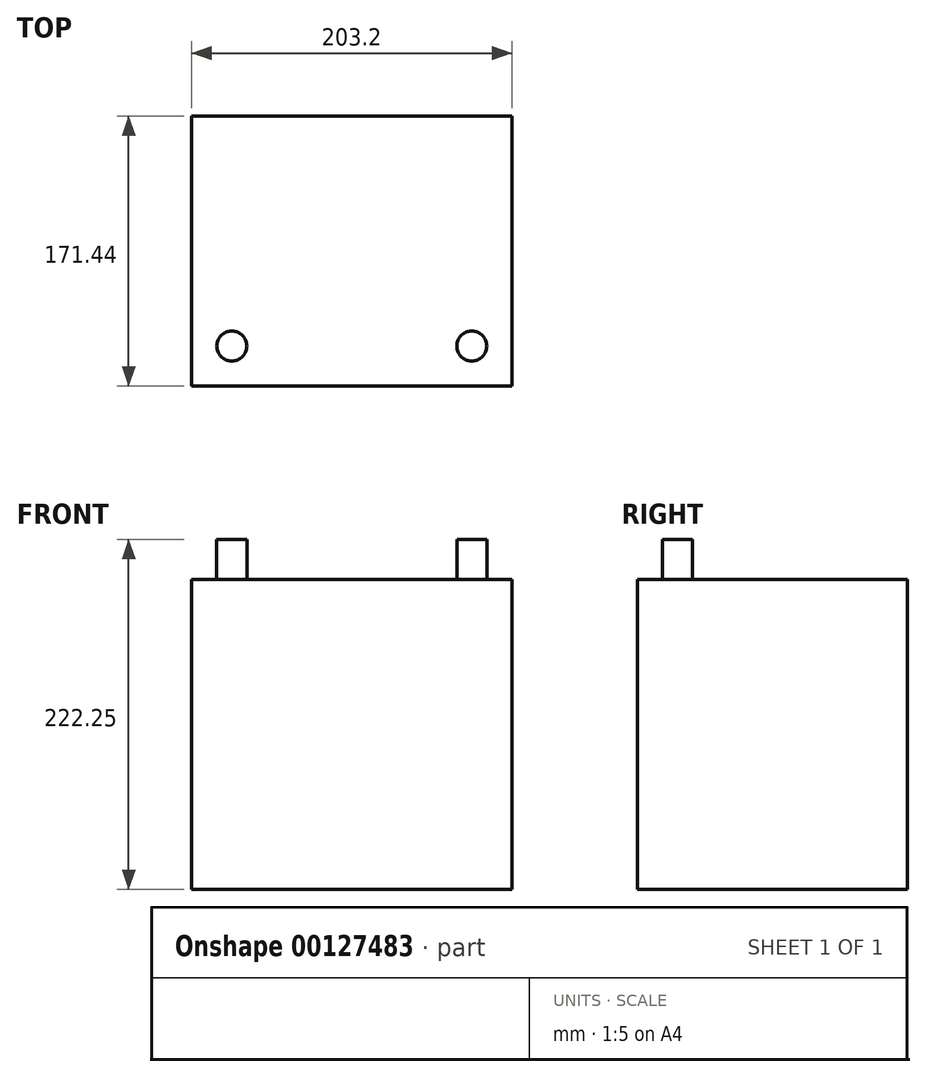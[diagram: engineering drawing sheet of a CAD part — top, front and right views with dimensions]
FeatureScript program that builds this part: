
annotation { "Feature Type Name" : "Feature", "Feature Type Description" : "" }
export const myFeature = defineFeature(function(context is Context, id is Id, definition is map)
    precondition{}
    {
        {
            var Q0;
            Q0=qCreatedBy(makeId("Top.planeOp"),FACE);
            var sketch = newSketch(context, id + "F0", { "sketchPlane" : qUnion([Q0])});
            skLineSegment(sketch, "E0.bottom", {"start": v(101.6, 85.73) * mm, "end": v(-101.6, 85.73) * mm});
            skLineSegment(sketch, "E0.top", {"start": v(101.6, -85.72) * mm, "end": v(-101.6, -85.72) * mm});
            skLineSegment(sketch, "E0.left", {"start": v(101.6, 85.72) * mm, "end": v(101.6, -85.72) * mm});
            skLineSegment(sketch, "E0.right", {"start": v(-101.6, 85.73) * mm, "end": v(-101.6, -85.72) * mm});
            skPoint(sketch, "E0.middle", {"position": v(0, 0) * mm});
            skSolve(sketch);
        }
        {
            var Q0;
            Q0 = qSketchRegion(id + "F0", true);
            extrude(context, id + "F1", {"entities" : qUnion([Q0]), "depth" : 196.85 * mm, "offsetDistance" : 25.4 * mm});
        }
        {
            var Q0;
            Q0=makeQuery(id+"F1.opExtrude","CAP_FACE",FACE,{"disambiguationData":[OSD([sQuery(id+"F0.wireOp",EDGE,"E0.bottom"),sQuery(id+"F0.wireOp",EDGE,"E0.top"),sQuery(id+"F0.wireOp",EDGE,"E0.left"),sQuery(id+"F0.wireOp",EDGE,"E0.right")])],"isStart":false});
            var sketch = newSketch(context, id + "F2", { "sketchPlane" : qUnion([Q0])});
            skCircle(sketch, "E1", {"center": v(-76.2, -60.32) * mm, "radius": 9.52 * mm});
            skLineSegment(sketch, "E2", {"start": v(0, 0) * mm, "end": v(0, -11.46) * mm, "construction": true});
            skCircle(sketch, "E3.MirrorC", {"center": v(76.2, -60.32) * mm, "radius": 9.52 * mm});
            skSolve(sketch);
        }
        {
            var Q0;
            Q0 = qSketchRegion(id + "F2", true);
            extrude(context, id + "F3", {"entities" : qUnion([Q0]), "operationType" : NewBodyOperationType.ADD, "depth" : 25.4 * mm, "offsetDistance" : 25.4 * mm});
        }
    });
